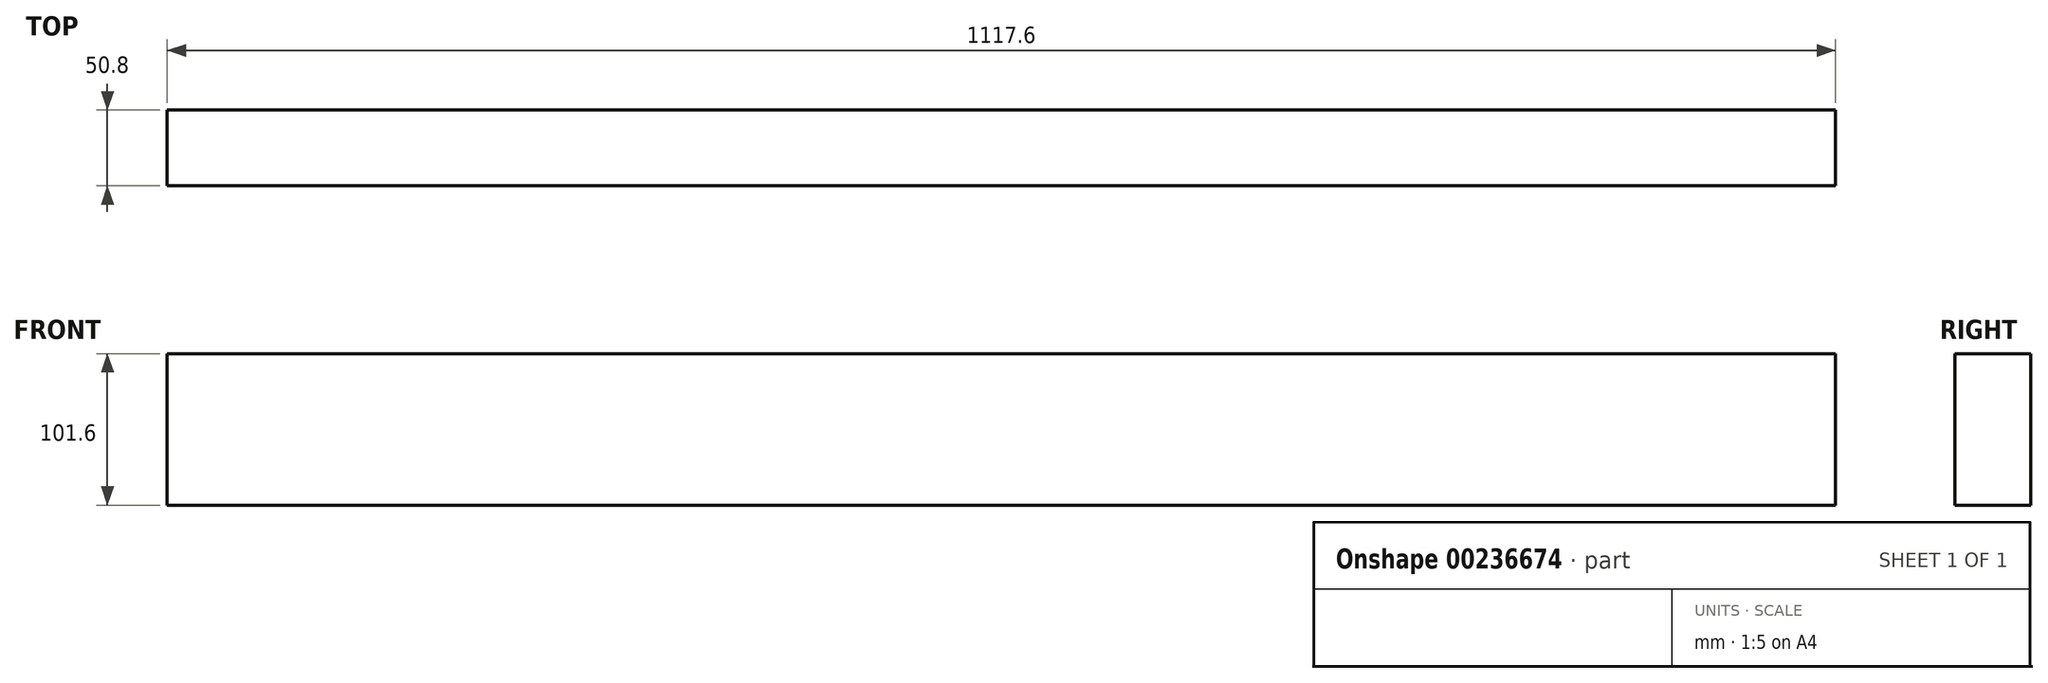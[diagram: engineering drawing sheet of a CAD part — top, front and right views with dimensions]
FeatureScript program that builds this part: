
annotation { "Feature Type Name" : "Feature", "Feature Type Description" : "" }
export const myFeature = defineFeature(function(context is Context, id is Id, definition is map)
    precondition{}
    {
        {
            var Q0;
            Q0=qCreatedBy(makeId("Front.planeOp"),FACE);
            var sketch = newSketch(context, id + "F0", { "sketchPlane" : qUnion([Q0])});
            skLineSegment(sketch, "E0.bottom", {"start": v(558.8, -50.8) * mm, "end": v(-558.8, -50.8) * mm});
            skLineSegment(sketch, "E0.top", {"start": v(558.8, 50.8) * mm, "end": v(-558.8, 50.8) * mm});
            skLineSegment(sketch, "E0.left", {"start": v(558.8, -50.8) * mm, "end": v(558.8, 50.8) * mm});
            skLineSegment(sketch, "E0.right", {"start": v(-558.8, -50.8) * mm, "end": v(-558.8, 50.8) * mm});
            skPoint(sketch, "E0.middle", {"position": v(0, 0) * mm});
            skSolve(sketch);
        }
        {
            var Q0;
            Q0 = qSketchRegion(id + "F0", true);
            extrude(context, id + "F1", {"entities" : qUnion([Q0]), "endBound" : BoundingType.SYMMETRIC, "depth" : 50.8 * mm});
        }
    });
